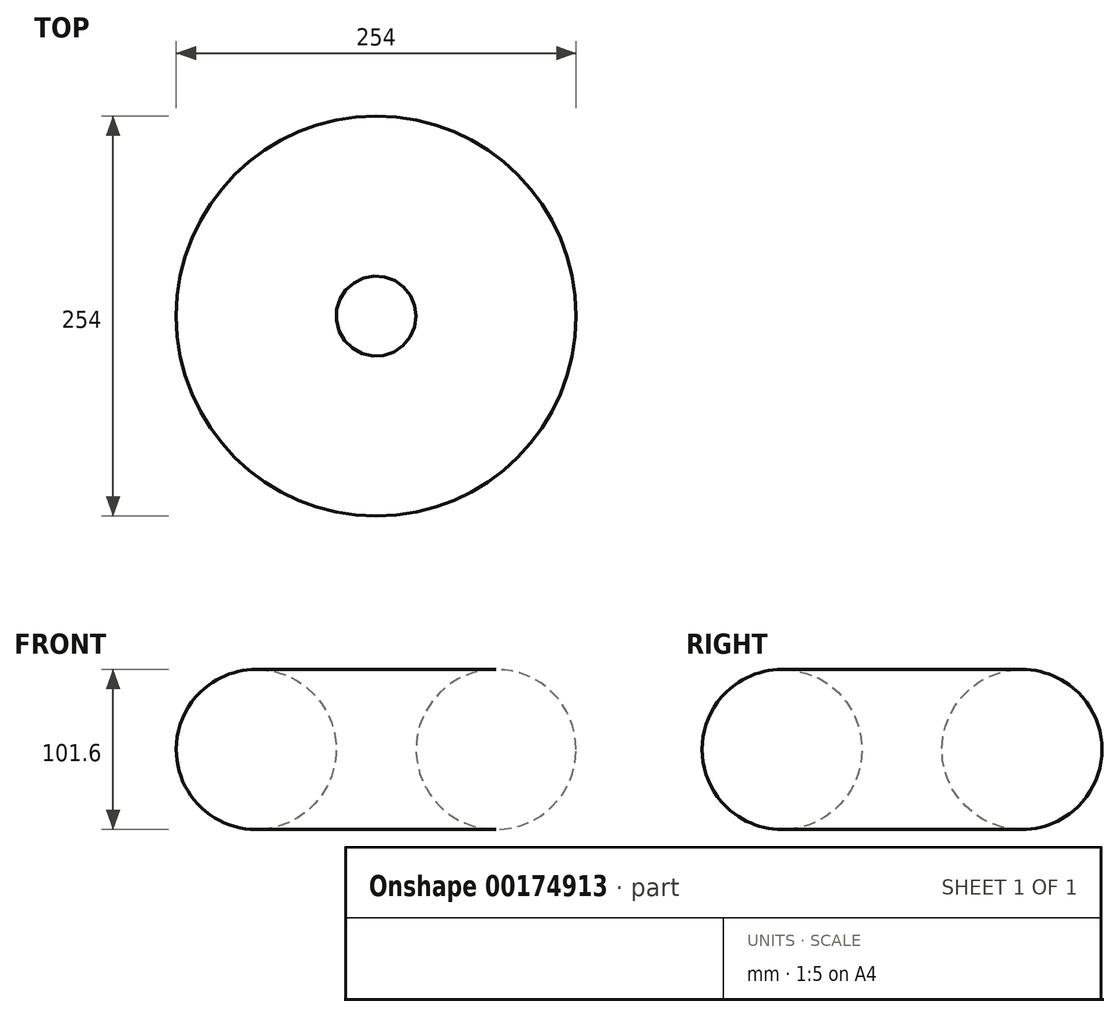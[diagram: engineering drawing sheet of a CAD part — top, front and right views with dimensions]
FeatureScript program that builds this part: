
annotation { "Feature Type Name" : "Feature", "Feature Type Description" : "" }
export const myFeature = defineFeature(function(context is Context, id is Id, definition is map)
    precondition{}
    {
        {
            var Q0;
            Q0=qCreatedBy(makeId("Front.planeOp"),FACE);
            var sketch = newSketch(context, id + "F0", { "sketchPlane" : qUnion([Q0])});
            skCircle(sketch, "E0", {"center": v(0, 0) * mm, "radius": 50.8 * mm});
            skLineSegment(sketch, "E1", {"start": v(76.2, 30.38) * mm, "end": v(76.2, -38.65) * mm});
            skSolve(sketch);
        }
        {
            var Q0;
            Q0=makeQuery(id+"F0.imprint","IMPRINT",FACE,{"disambiguationData":[TD([[makeQuery(id+"F0.imprint","IMPRINT",EDGE,{"derivedFrom":sQuery(id+"F0.wireOp",EDGE,"E0")}),1.0]])]});
            var Q1;
            Q1=sQuery(id+"F0.wireOp",EDGE,"E1");
            revolve(context, id + "F1", {"entities" : qUnion([Q0]), "axis" : qUnion([Q1]), "revolveType" : RevolveType.FULL});
        }
    });
